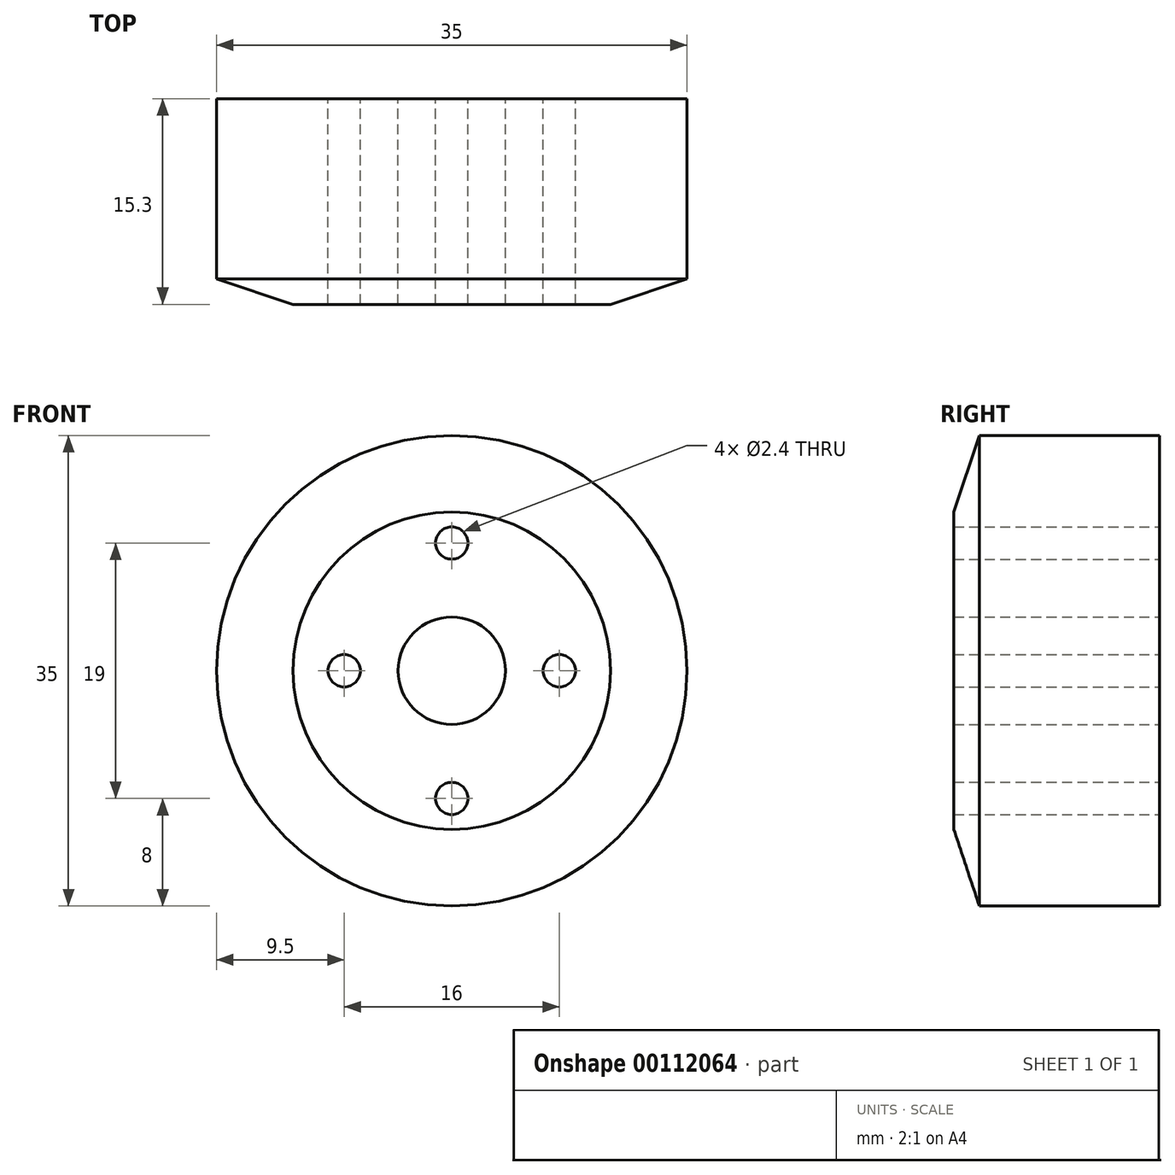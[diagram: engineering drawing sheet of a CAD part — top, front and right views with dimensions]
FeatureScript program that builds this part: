
annotation { "Feature Type Name" : "Feature", "Feature Type Description" : "" }
export const myFeature = defineFeature(function(context is Context, id is Id, definition is map)
    precondition{}
    {
        {
            var Q0;
            Q0=qCreatedBy(makeId("Front.planeOp"),FACE);
            var sketch = newSketch(context, id + "F0", { "sketchPlane" : qUnion([Q0])});
            skCircle(sketch, "E0", {"center": v(0, 0) * mm, "radius": 17.5 * mm});
            skCircle(sketch, "E1", {"center": v(0, 0) * mm, "radius": 4 * mm});
            skSolve(sketch);
        }
        {
            var Q0;
            Q0 = qSketchRegion(id + "F0", true);
            extrude(context, id + "F1", {"entities" : qUnion([Q0]), "depth" : 15.3 * mm});
        }
        {
            var Q0;
            Q0=makeQuery(id+"F1.opExtrude","CAP_EDGE",EDGE,{"disambiguationData":[OSD([sQuery(id+"F0.wireOp",EDGE,"E0")])],"isStart":false});
            chamfer(context, id + "F2", {"entities" : qUnion([Q0]), "chamferType" : ChamferType.TWO_OFFSETS, "width1" : 5.7 * mm, "oppositeDirection" : false, "width2" : 1.9 * mm, "tangentPropagation" : true});
        }
        {
            var Q0;
            Q0=makeQuery(id+"F1.opExtrude","CAP_FACE",FACE,{"disambiguationData":[OSD([sQuery(id+"F0.wireOp",EDGE,"E0"),sQuery(id+"F0.wireOp",EDGE,"E1")])],"isStart":false});
            var sketch = newSketch(context, id + "F3", { "sketchPlane" : qUnion([Q0])});
            skCircle(sketch, "E2", {"center": v(0, 9.5) * mm, "radius": 1.5 * mm});
            skCircle(sketch, "E3", {"center": v(0, -9.5) * mm, "radius": 1.5 * mm});
            skCircle(sketch, "E4", {"center": v(-8, 0) * mm, "radius": 1.5 * mm});
            skCircle(sketch, "E5", {"center": v(8, 0) * mm, "radius": 1.5 * mm});
            skSolve(sketch);
        }
        {
            var Q0;
            Q0=sQuery(id+"F3.wireOp",VERTEX,"E2.center");
            var Q1;
            Q1=sQuery(id+"F3.wireOp",VERTEX,"E4.center");
            var Q2;
            Q2=sQuery(id+"F3.wireOp",VERTEX,"E3.center");
            var Q3;
            Q3=sQuery(id+"F3.wireOp",VERTEX,"E5.center");
            var Q4;
            Q4=makeQuery(id+"F1.opExtrude","SWEPT_BODY",BODY,{"disambiguationData":[OSD([sQuery(id+"F0.wireOp",EDGE,"E0"),sQuery(id+"F0.wireOp",EDGE,"E1")])]});
            hole(context, id + "F4", {"style" : HoleStyle.SIMPLE, "endStyle" : HoleEndStyle.THROUGH, "standardTappedOrClearance" : lookupTablePath({ "standard" : "ISO", "engagement" : "75%", "pitch" : "0.6 mm", "size" : "M3", "type" : "Tapped" }), "standardBlindInLast" : lookupTablePath({ "standard" : "ISO", "engagement" : "75%", "pitch" : "0.6 mm", "size" : "M3", "type" : "Tapped" }), "holeDiameter" : 2.4 * mm, "locations" : qUnion([Q0, Q1, Q2, Q3]), "scope" : qUnion([Q4]), "isTappedThrough" : true, "showTappedDepth" : true});
        }
    });
